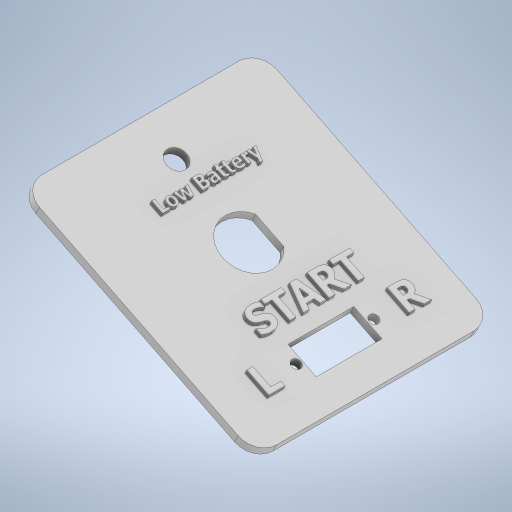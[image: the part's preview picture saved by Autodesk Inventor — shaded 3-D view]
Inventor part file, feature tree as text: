
AUTODESK INVENTOR PART (.ipt)
format: ipt  version: 2024.2 (Build 282272000, 272)  size: 839,168 bytes
history: native  units: mm
features: sketch x10, extrude x9, projected_geometry x4, fillet x2, emboss x1
ambient origin geometry x8: Origin, YZ Plane, XZ Plane, XY Plane, X Axis, Y Axis, Z Axis, Center Point
bodies: Solid1 (feature_tree)
feature tree (26):
  extrude  "Extrusion1"  Depth=2.0mm
  extrude  "Extrusion2"  Depth=6.5mm
  extrude  "Extrusion3"  Depth=9.0mm TaperAngle=0.0deg
  extrude  "Extrusion5"  Depth=9.0mm TaperAngle=0.0deg
  emboss  "Emboss1"
  extrude  "Extrusion6"  Depth=20.0mm
  extrude  "Extrusion7"  Depth=5.0mm
  extrude  "Extrusion8"  Depth=16.3mm
  extrude  "Extrusion9"  Depth=10.0mm
  fillet  "Fillet1"  Radius=20.0mm
  extrude  "Extrusion10"  Depth=8.15mm
  fillet  "Fillet2"  Radius=20.0mm
  sketch  "Sketch2"  dims[d4=2.0mm d5=2.0mm]
  sketch  "Sketch3"  dims[d6=38.25mm d8=6.5mm]
  projected_geometry  "Projected Loop1"
  sketch  "Sketch4"  dims[d9=8.0mm d10=9.0mm d11=0.0mm]
  projected_geometry  "Projected Loop2"
  projected_geometry  "Projected Loop3"
  projected_geometry  "Projected Loop4"
  sketch  "Sketch7"  dims[d12=41.0mm d13=0.0mm d14=9.0mm d15=0.0mm]
  sketch  "Sketch8"  dims[d16=15.0mm d29=20.0mm]
  sketch  "Sketch9"  dims[d30=5.0mm d31=13.0mm]
  sketch  "Sketch10"  dims[d32=29.5mm d33=16.3mm]
  sketch  "Sketch11"  dims[d34=5.2mm d35=10.0mm d36=20.0mm]
  sketch  "Sketch12"  dims[d37=7.8mm d38=8.15mm d39=20.0mm]
  sketch  "Sketch13"  dims[d40=0.0mm d41=0.0mm d42=1.0mm d43=0.0mm d44=49.0mm d45=3.0mm d46=3.0mm d47=3.25mm d48=3.25mm d49=4.0mm d50=2.5mm d51=0.0mm d52=3.0mm d53=3.0mm d54=51.0mm d55=4.0mm d56=4.0mm d57=2.5mm d58=0.0mm d59=135.0deg d60=20.0mm d61=135.0deg d62=20.0mm d63=65.018mm d64=0.0mm d65=0.0mm d66=0.0mm d67=2.3mm d68=2.3mm d69=1.5mm d70=1.5mm d71=3.9mm d72=3.9mm d73=5.0mm d74=4.0mm d75=4.0mm d76=47.0mm d78=48.0mm d79=46.0mm d81=1.0mm d82=12.0mm d83=1.58mm d84=1.5mm d85=0.0mm d86=2.0mm]
